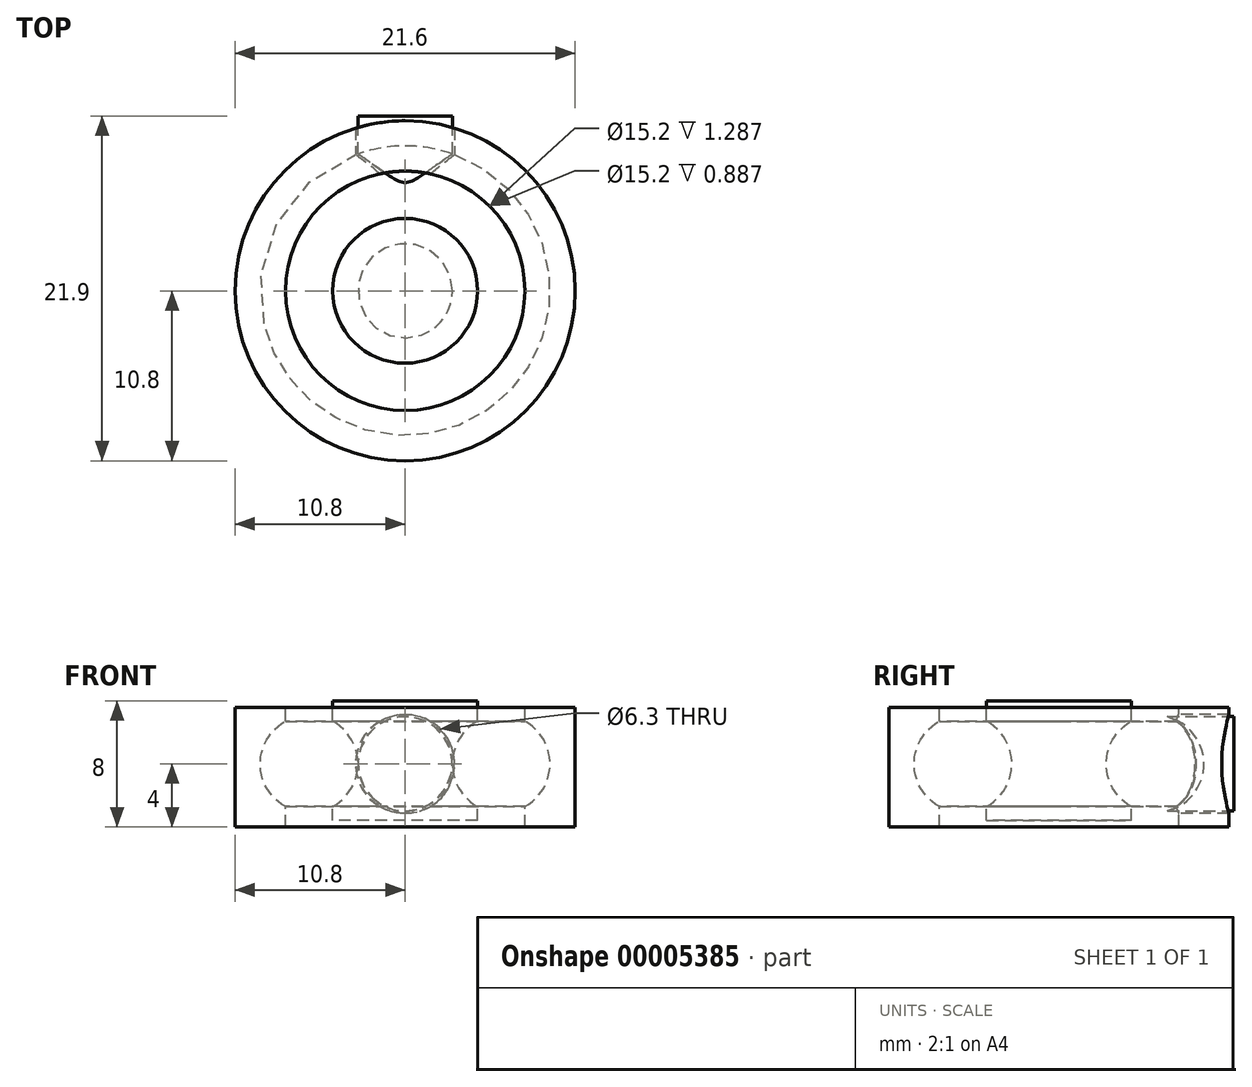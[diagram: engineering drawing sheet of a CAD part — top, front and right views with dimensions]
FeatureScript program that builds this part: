
annotation { "Feature Type Name" : "Feature", "Feature Type Description" : "" }
export const myFeature = defineFeature(function(context is Context, id is Id, definition is map)
    precondition{}
    {
        {
            var Q0;
            Q0=qCreatedBy(makeId("Top.planeOp"),FACE);
            var sketch = newSketch(context, id + "F0", { "sketchPlane" : qUnion([Q0])});
            skArc(sketch, "E0", {"start": v(3, 0) * mm, "mid": v(0, 3) * mm, "end": v(-3, 0) * mm});
            skLineSegment(sketch, "E1", {"start": v(3, 0) * mm, "end": v(-3, 0) * mm});
            skLineSegment(sketch, "E2", {"start": v(0, 0) * mm, "end": v(0, -6.1) * mm, "construction": true});
            skSolve(sketch);
        }
        {
            var Q0;
            Q0=qCreatedBy(makeId("Right.planeOp"),FACE);
            var sketch = newSketch(context, id + "F1", { "sketchPlane" : qUnion([Q0])});
            skCircle(sketch, "E3", {"center": v(0, 0) * mm, "radius": 3.1 * mm});
            skLineSegment(sketch, "E4", {"start": v(0, 0) * mm, "end": v(-12.4, 0) * mm, "construction": true});
            skLineSegment(sketch, "E5", {"start": v(-12.4, 8.14) * mm, "end": v(-12.4, -5.03) * mm, "construction": true});
            skLineSegment(sketch, "E6", {"start": v(0, 0) * mm, "end": v(0, 3.76) * mm, "construction": true});
            skLineSegment(sketch, "E7", {"start": v(-6.1, 3.76) * mm, "end": v(-6.1, -2.41) * mm, "construction": true});
            skSolve(sketch);
        }
        {
            var Q0;
            Q0=sQuery(id+"F1.wireOp",EDGE,"E3");
            var Q1;
            Q1=sQuery(id+"F1.wireOp",EDGE,"E7");
            revolve(context, id + "F2", {"bodyType" : ToolBodyType.SURFACE, "surfaceEntities" : qUnion([Q0]), "axis" : qUnion([Q1]), "revolveType" : RevolveType.FULL});
        }
        {
            var Q0;
            Q0=qCreatedBy(makeId("Right.planeOp"),FACE);
            var sketch = newSketch(context, id + "F3", { "sketchPlane" : qUnion([Q0])});
            skCircle(sketch, "E8.0", {"center": v(0, 0) * mm, "radius": 3.1 * mm});
            skLineSegment(sketch, "E9.0", {"start": v(-6.1, 3.76) * mm, "end": v(-6.1, -2.41) * mm});
            skLineSegment(sketch, "E9.1", {"start": v(0, 0) * mm, "end": v(-12.4, 0) * mm});
            skPoint(sketch, "E10.rect.middle", {"position": v(-6.1, 0) * mm});
            skLineSegment(sketch, "E11", {"start": v(-1.5, 4) * mm, "end": v(-1.5, -3.6) * mm});
            skLineSegment(sketch, "E12", {"start": v(-1.5, -3.6) * mm, "end": v(-6.1, -3.6) * mm});
            skLineSegment(sketch, "E13", {"start": v(-6.1, -3.6) * mm, "end": v(-6.1, 4) * mm});
            skLineSegment(sketch, "E14", {"start": v(-6.1, 4) * mm, "end": v(-1.5, 4) * mm});
            skLineSegment(sketch, "E15", {"start": v(4.7, 3.6) * mm, "end": v(4.7, -4) * mm});
            skLineSegment(sketch, "E16", {"start": v(4.7, -4) * mm, "end": v(1.5, -4) * mm});
            skLineSegment(sketch, "E17", {"start": v(4.7, 3.6) * mm, "end": v(1.5, 3.6) * mm});
            skLineSegment(sketch, "E18", {"start": v(1.5, 3.6) * mm, "end": v(1.5, -4) * mm});
            skSolve(sketch);
        }
        {
            var Q0;
            {var subQ0=sQuery(id+"F3.wireOp",EDGE,"E14");Q0=makeQuery(id+"F3.imprint","IMPRINT",FACE,{"disambiguationData":[TD([[makeQuery(id+"F3.imprint","IMPRINT",EDGE,{"derivedFrom":subQ0}),-1.0]])]});}
            var Q1;
            {var subQ3=sQuery(id+"F3.wireOp",EDGE,"E12");Q1=makeQuery(id+"F3.imprint","IMPRINT",FACE,{"disambiguationData":[TD([[makeQuery(id+"F3.imprint","IMPRINT",EDGE,{"derivedFrom":subQ3}),-1.0]])]});}
            var Q2;
            Q2=sQuery(id+"F3.wireOp",EDGE,"E9.0");
            revolve(context, id + "F4", {"entities" : qUnion([Q0, Q1]), "axis" : qUnion([Q2]), "revolveType" : RevolveType.FULL});
        }
        {
            var Q0;
            Q0=makeQuery(id+"F3.imprint","IMPRINT",FACE,{"disambiguationData":[TD([[makeQuery(id+"F3.imprint","IMPRINT",EDGE,{"derivedFrom":sQuery(id+"F3.wireOp",EDGE,"E15")}),-1.0]])]});
            var Q1;
            Q1=sQuery(id+"F3.wireOp",EDGE,"E9.0");
            revolve(context, id + "F5", {"entities" : qUnion([Q0]), "axis" : qUnion([Q1]), "revolveType" : RevolveType.FULL});
        }
        {
            var Q0;
            Q0=qCreatedBy(makeId("Front.planeOp"),FACE);
            var sketch = newSketch(context, id + "F6", { "sketchPlane" : qUnion([Q0])});
            skCircle(sketch, "E19", {"center": v(0, 0) * mm, "radius": 3.15 * mm});
            skSolve(sketch);
        }
        {
            var Q0;
            Q0=makeQuery(id+"F6.imprint","IMPRINT",FACE,{"disambiguationData":[TD([[makeQuery(id+"F6.imprint","IMPRINT",EDGE,{"derivedFrom":sQuery(id+"F6.wireOp",EDGE,"E19")}),1.0]])]});
            var Q1;
            Q1=makeQuery(id+"F5.opRevolve","SWEPT_FACE",FACE,{"disambiguationData":[OSD([sQuery(id+"F3.wireOp",EDGE,"E15")])]});
            extrude(context, id + "F7", {"entities" : qUnion([Q0]), "operationType" : NewBodyOperationType.REMOVE, "endBound" : BoundingType.UP_TO_SURFACE, "oppositeDirection" : true, "endBoundEntityFace" : qUnion([Q1]), "depth" : 25 * mm});
        }
        {
            var Q0;
            Q0=qCreatedBy(makeId("Front.planeOp"),FACE);
            var sketch = newSketch(context, id + "F8", { "sketchPlane" : qUnion([Q0])});
            skLineSegment(sketch, "E20.rect.bottom", {"start": v(13.05, 1.97) * mm, "end": v(8.99, 1.97) * mm});
            skLineSegment(sketch, "E20.rect.top", {"start": v(13.05, 8.89) * mm, "end": v(8.99, 8.89) * mm});
            skLineSegment(sketch, "E20.rect.left", {"start": v(13.05, 1.97) * mm, "end": v(13.05, 8.89) * mm});
            skLineSegment(sketch, "E20.rect.right", {"start": v(8.99, 1.97) * mm, "end": v(8.99, 8.89) * mm});
            skPoint(sketch, "E20.rect.middle", {"position": v(11.02, 5.43) * mm});
            skSolve(sketch);
        }
        {
            var Q0;
            Q0=makeQuery(id+"F8.imprint","IMPRINT",FACE,{"disambiguationData":[TD([[makeQuery(id+"F8.imprint","IMPRINT",EDGE,{"derivedFrom":sQuery(id+"F8.wireOp",EDGE,"E20.rect.bottom")}),-1.0]])]});
            cPlane(context, id + "F9", {"entities" : qUnion([Q0]), "cplaneType" : CPlaneType.OFFSET, "offset" : 5 * mm, "oppositeDirection" : true, "width" : 150 * mm, "height" : 150 * mm});
        }
        {
            var Q0;
            Q0=qCreatedBy(id+"F9.planeOp",FACE);
            var sketch = newSketch(context, id + "F10", { "sketchPlane" : qUnion([Q0])});
            skCircle(sketch, "E21", {"center": v(0, 0) * mm, "radius": 3 * mm});
            skSolve(sketch);
        }
        {
            var Q0;
            Q0=makeQuery(id+"F10.imprint","IMPRINT",FACE,{"disambiguationData":[TD([[makeQuery(id+"F10.imprint","IMPRINT",EDGE,{"derivedFrom":sQuery(id+"F10.wireOp",EDGE,"E21")}),1.0]])]});
            var Q1;
            Q1=makeQuery(id+"F5.opRevolve","SWEPT_FACE",FACE,{"disambiguationData":[OSD([sQuery(id+"F3.wireOp",EDGE,"E8.0")])]});
            extrude(context, id + "F11", {"entities" : qUnion([Q0]), "endBound" : BoundingType.UP_TO_SURFACE, "endBoundEntityFace" : qUnion([Q1]), "depth" : 25 * mm});
        }
    });
